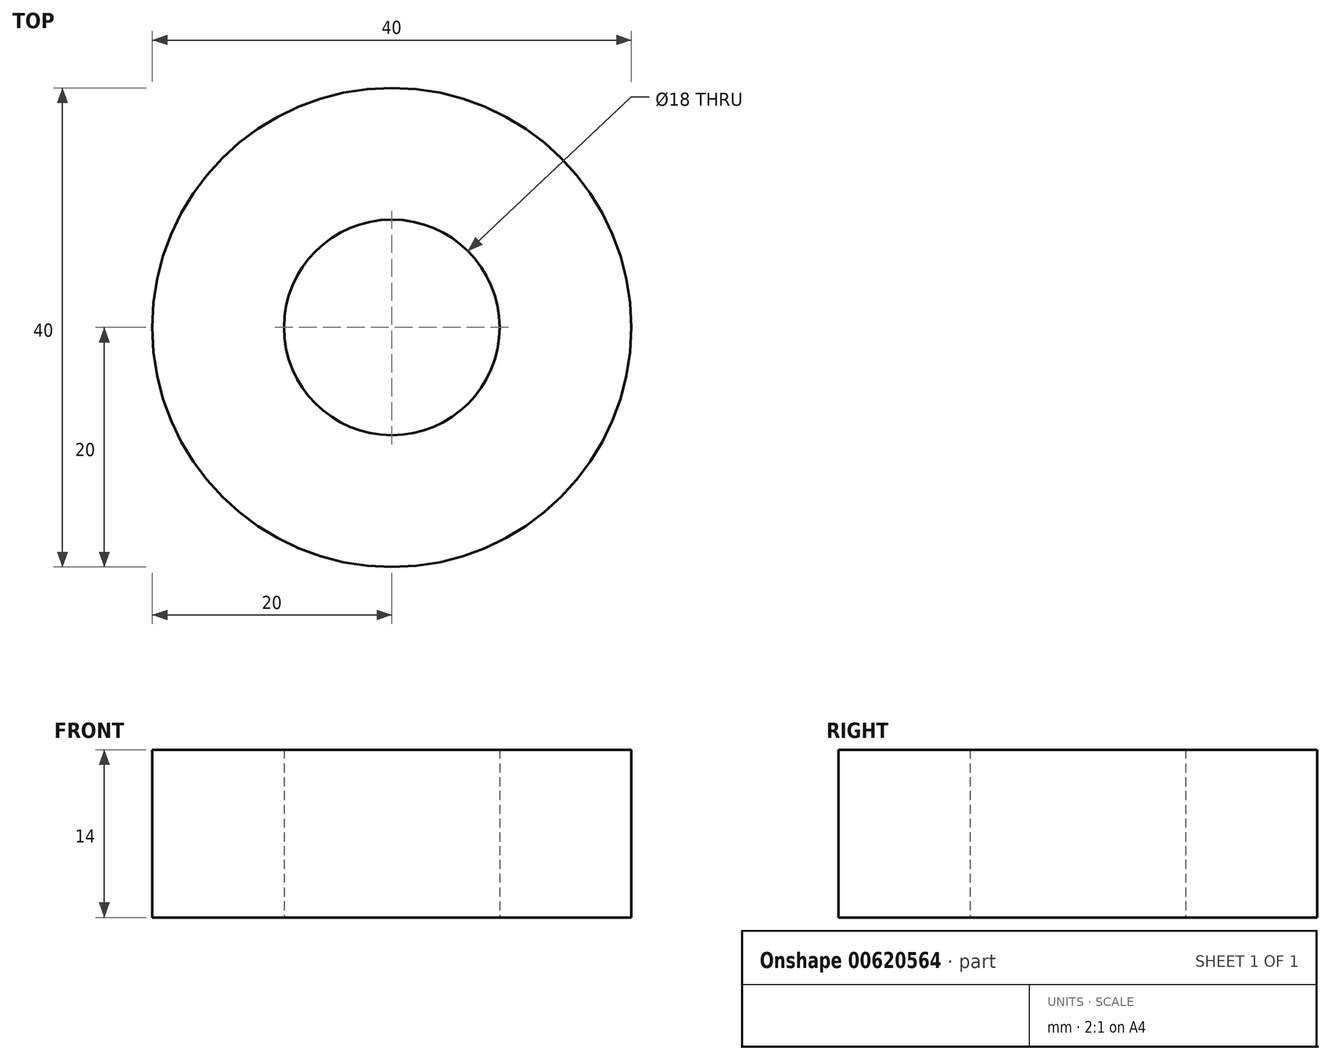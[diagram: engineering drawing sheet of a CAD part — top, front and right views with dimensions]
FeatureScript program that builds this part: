
annotation { "Feature Type Name" : "Feature", "Feature Type Description" : "" }
export const myFeature = defineFeature(function(context is Context, id is Id, definition is map)
    precondition{}
    {
        {
            var Q0;
            Q0=qCreatedBy(makeId("Top.planeOp"),FACE);
            var sketch = newSketch(context, id + "F0", { "sketchPlane" : qUnion([Q0])});
            skCircle(sketch, "E0", {"center": v(0, 0) * mm, "radius": 20 * mm});
            skCircle(sketch, "E1", {"center": v(0, 0) * mm, "radius": 9 * mm});
            skSolve(sketch);
        }
        {
            var Q0;
            Q0 = qSketchRegion(id + "F0", true);
            extrude(context, id + "F1", {"entities" : qUnion([Q0]), "depth" : 14 * mm, "offsetDistance" : 25 * mm});
        }
    });
